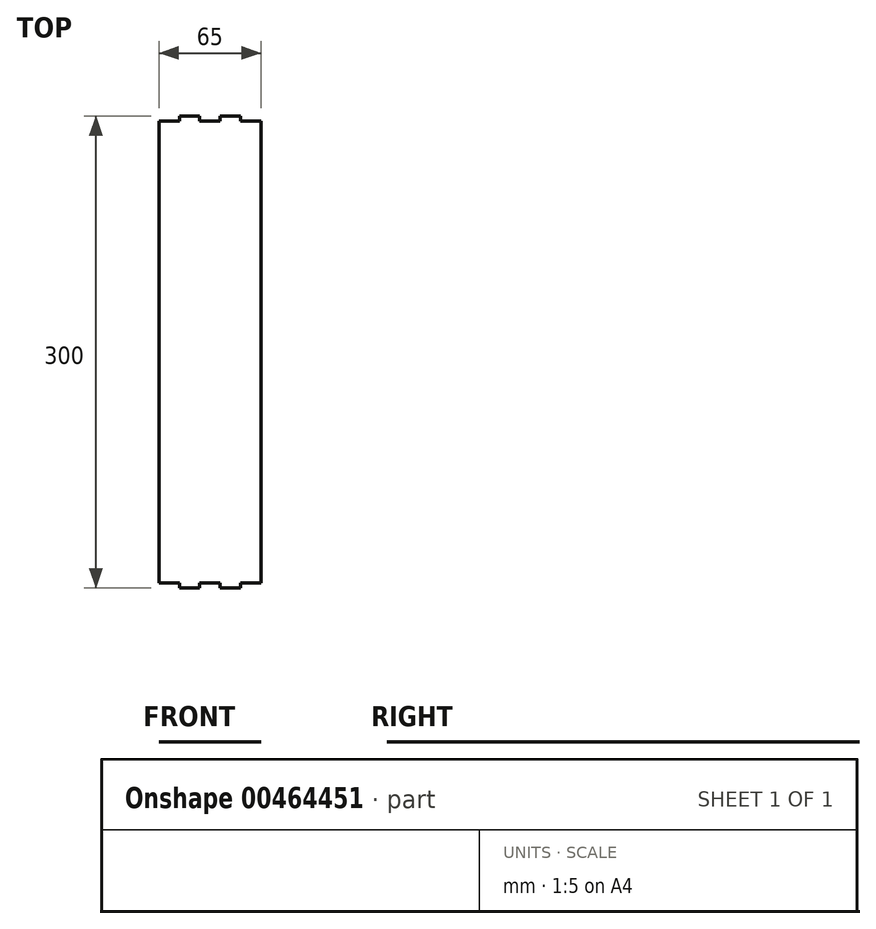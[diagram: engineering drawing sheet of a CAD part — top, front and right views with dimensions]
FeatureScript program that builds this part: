
annotation { "Feature Type Name" : "Feature", "Feature Type Description" : "" }
export const myFeature = defineFeature(function(context is Context, id is Id, definition is map)
    precondition{}
    {
        {
            var Q0;
            Q0=qCreatedBy(makeId("Top.planeOp"),FACE);
            var sketch = newSketch(context, id + "F0", { "sketchPlane" : qUnion([Q0])});
            skLineSegment(sketch, "E0.bottom", {"start": v(-32.5, 150) * mm, "end": v(32.5, 150) * mm});
            skLineSegment(sketch, "E0.top", {"start": v(-32.5, -150) * mm, "end": v(32.5, -150) * mm});
            skLineSegment(sketch, "E0.left", {"start": v(-32.5, 150) * mm, "end": v(-32.5, -150) * mm});
            skLineSegment(sketch, "E0.right", {"start": v(32.5, 150) * mm, "end": v(32.5, -150) * mm});
            skSolve(sketch);
        }
        {
            var Q0;
            Q0 = qSketchRegion(id + "F0", true);
            extrude(context, id + "F1", {"entities" : qUnion([Q0]), "depth" : 1 / 203.2 * mm});
        }
        {
            var Q0;
            Q0=makeQuery(id+"F1.opExtrude","CAP_FACE",FACE,{"disambiguationData":[OSD([sQuery(id+"F0.wireOp",EDGE,"E0.bottom"),sQuery(id+"F0.wireOp",EDGE,"E0.top"),sQuery(id+"F0.wireOp",EDGE,"E0.left"),sQuery(id+"F0.wireOp",EDGE,"E0.right")])],"isStart":false});
            var sketch = newSketch(context, id + "F2", { "sketchPlane" : qUnion([Q0])});
            skLineSegment(sketch, "E1.bottom", {"start": v(-32.5, -150) * mm, "end": v(-19.5, -150) * mm});
            skLineSegment(sketch, "E1.top", {"start": v(-32.5, -146.82) * mm, "end": v(-19.5, -146.82) * mm});
            skLineSegment(sketch, "E1.left", {"start": v(-32.5, -150) * mm, "end": v(-32.5, -146.82) * mm});
            skLineSegment(sketch, "E1.right", {"start": v(-19.5, -150) * mm, "end": v(-19.5, -146.82) * mm});
            skLineSegment(sketch, "E2.0.1.0", {"start": v(-32.5, 146.83) * mm, "end": v(-19.5, 146.83) * mm});
            skLineSegment(sketch, "E2.0.1.1", {"start": v(-32.5, 150) * mm, "end": v(-19.5, 150) * mm});
            skLineSegment(sketch, "E2.0.1.2", {"start": v(-32.5, 146.83) * mm, "end": v(-32.5, 150) * mm});
            skLineSegment(sketch, "E2.0.1.3", {"start": v(-19.5, 146.83) * mm, "end": v(-19.5, 150) * mm});
            skLineSegment(sketch, "E2.1.0.0", {"start": v(-6.5, -150) * mm, "end": v(6.5, -150) * mm});
            skLineSegment(sketch, "E2.1.0.1", {"start": v(-6.5, -146.82) * mm, "end": v(6.5, -146.82) * mm});
            skLineSegment(sketch, "E2.1.0.2", {"start": v(-6.5, -150) * mm, "end": v(-6.5, -146.82) * mm});
            skLineSegment(sketch, "E2.1.0.3", {"start": v(6.5, -150) * mm, "end": v(6.5, -146.82) * mm});
            skLineSegment(sketch, "E2.1.1.0", {"start": v(-6.5, 146.83) * mm, "end": v(6.5, 146.83) * mm});
            skLineSegment(sketch, "E2.1.1.1", {"start": v(-6.5, 150) * mm, "end": v(6.5, 150) * mm});
            skLineSegment(sketch, "E2.1.1.2", {"start": v(-6.5, 146.83) * mm, "end": v(-6.5, 150) * mm});
            skLineSegment(sketch, "E2.1.1.3", {"start": v(6.5, 146.83) * mm, "end": v(6.5, 150) * mm});
            skLineSegment(sketch, "E2.2.0.0", {"start": v(19.5, -150) * mm, "end": v(32.5, -150) * mm});
            skLineSegment(sketch, "E2.2.0.1", {"start": v(19.5, -146.82) * mm, "end": v(32.5, -146.82) * mm});
            skLineSegment(sketch, "E2.2.0.2", {"start": v(19.5, -150) * mm, "end": v(19.5, -146.82) * mm});
            skLineSegment(sketch, "E2.2.0.3", {"start": v(32.5, -150) * mm, "end": v(32.5, -146.82) * mm});
            skLineSegment(sketch, "E2.2.1.0", {"start": v(19.5, 146.83) * mm, "end": v(32.5, 146.83) * mm});
            skLineSegment(sketch, "E2.2.1.1", {"start": v(19.5, 150) * mm, "end": v(32.5, 150) * mm});
            skLineSegment(sketch, "E2.2.1.2", {"start": v(19.5, 146.83) * mm, "end": v(19.5, 150) * mm});
            skLineSegment(sketch, "E2.2.1.3", {"start": v(32.5, 146.83) * mm, "end": v(32.5, 150) * mm});
            skLineSegment(sketch, "E2.direction1", {"start": v(-32.5, -150) * mm, "end": v(-6.5, -150) * mm, "construction": true});
            skLineSegment(sketch, "E2.direction2", {"start": v(-32.5, -150) * mm, "end": v(-32.5, 146.83) * mm, "construction": true});
            skSolve(sketch);
        }
        {
            var Q0;
            Q0 = qSketchRegion(id + "F2", true);
            extrude(context, id + "F3", {"entities" : qUnion([Q0]), "operationType" : NewBodyOperationType.REMOVE, "endBound" : BoundingType.THROUGH_ALL, "oppositeDirection" : true, "depth" : 25 * mm});
        }
    });
